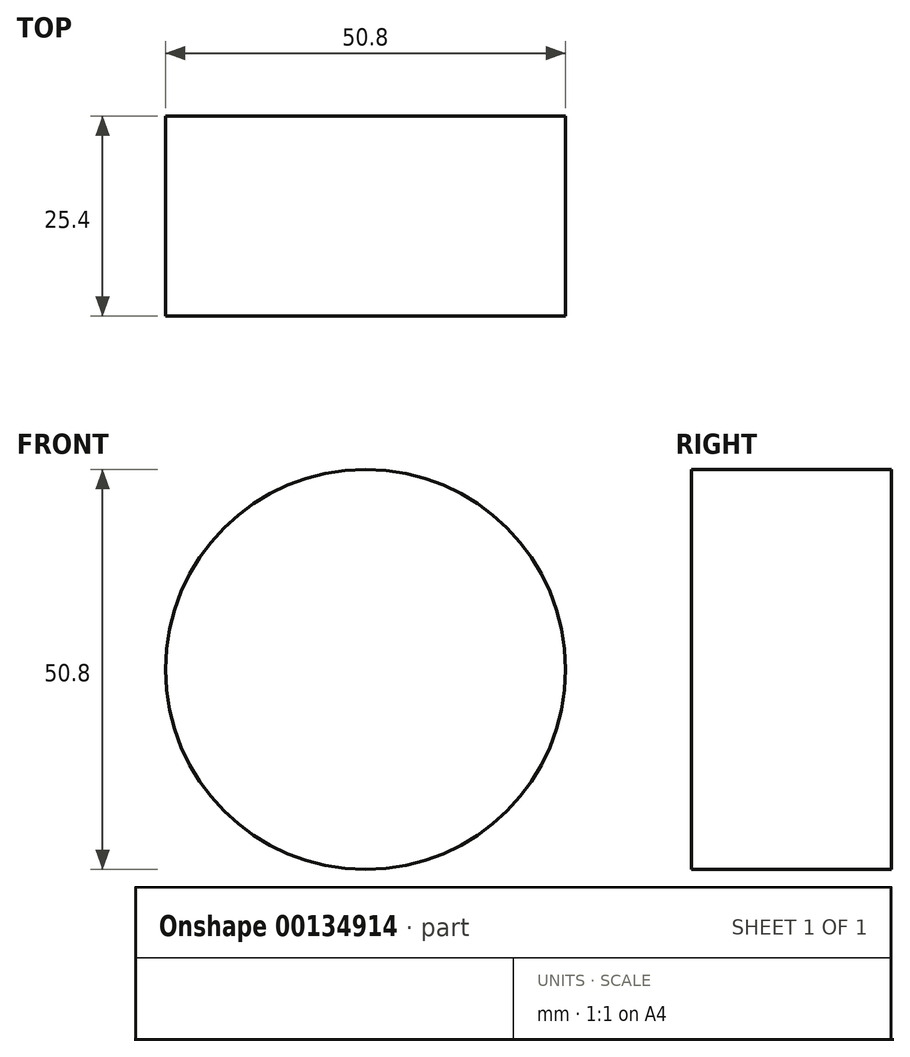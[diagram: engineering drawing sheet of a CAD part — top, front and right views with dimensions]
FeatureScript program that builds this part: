
annotation { "Feature Type Name" : "Feature", "Feature Type Description" : "" }
export const myFeature = defineFeature(function(context is Context, id is Id, definition is map)
    precondition{}
    {
        {
            var Q0;
            Q0=qCreatedBy(makeId("Front.planeOp"),FACE);
            var sketch = newSketch(context, id + "F0", { "sketchPlane" : qUnion([Q0])});
            skCircle(sketch, "E0", {"center": v(0, 0) * mm, "radius": 25.4 * mm});
            skSolve(sketch);
        }
        {
            var Q0;
            Q0 = qSketchRegion(id + "F0", true);
            extrude(context, id + "F1", {"entities" : qUnion([Q0]), "depth" : 25.4 * mm});
        }
    });
